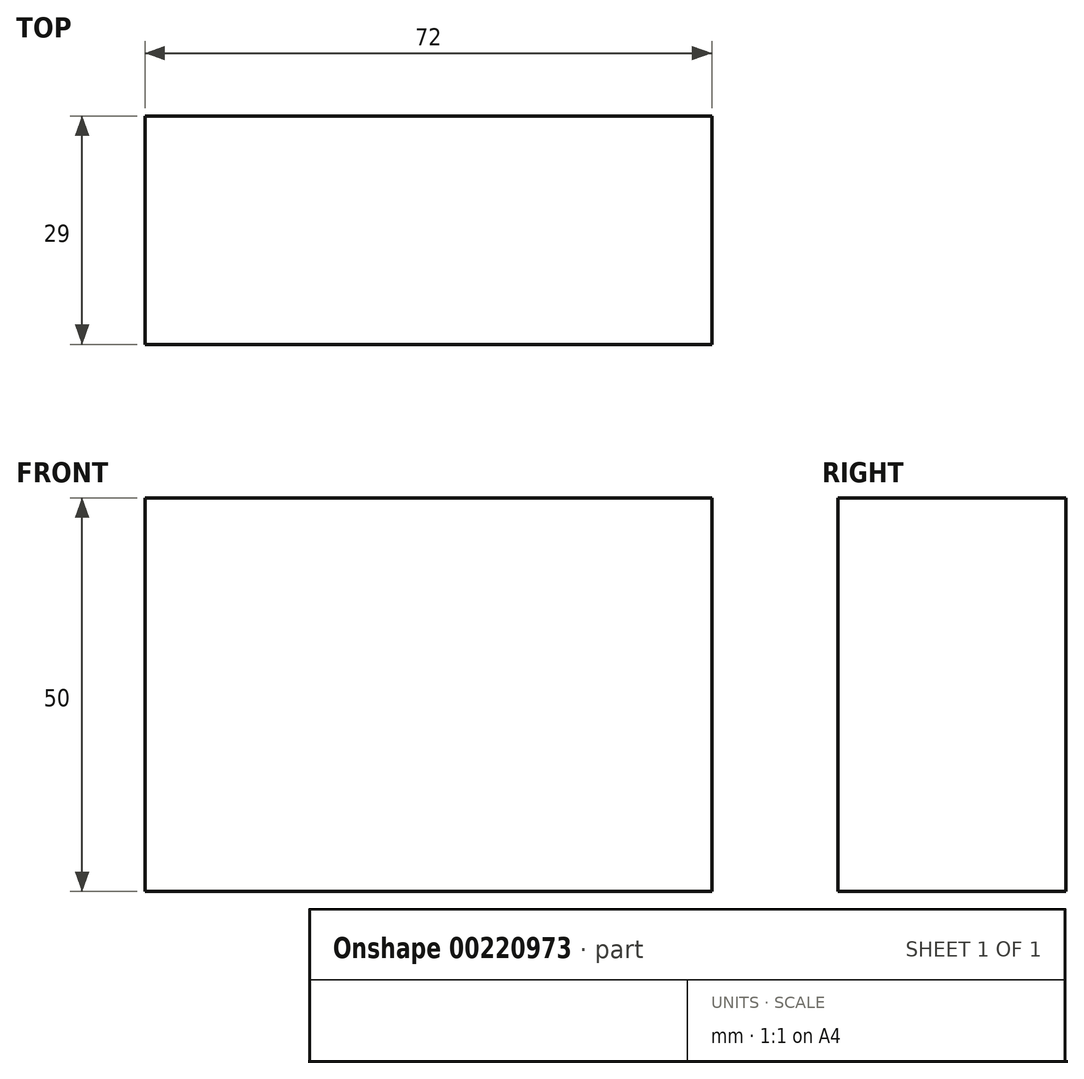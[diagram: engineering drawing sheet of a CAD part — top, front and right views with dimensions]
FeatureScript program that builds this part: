
annotation { "Feature Type Name" : "Feature", "Feature Type Description" : "" }
export const myFeature = defineFeature(function(context is Context, id is Id, definition is map)
    precondition{}
    {
        {
            var Q0;
            Q0=qCreatedBy(makeId("Front.planeOp"),FACE);
            var sketch = newSketch(context, id + "F0", { "sketchPlane" : qUnion([Q0])});
            skLineSegment(sketch, "E0.bottom", {"start": v(0, 0) * mm, "end": v(72, 0) * mm});
            skLineSegment(sketch, "E0.top", {"start": v(0, 50) * mm, "end": v(72, 50) * mm});
            skLineSegment(sketch, "E0.left", {"start": v(0, 0) * mm, "end": v(0, 50) * mm});
            skLineSegment(sketch, "E0.right", {"start": v(72, 0) * mm, "end": v(72, 50) * mm});
            skSolve(sketch);
        }
        {
            var Q0;
            Q0 = qSketchRegion(id + "F0", true);
            extrude(context, id + "F1", {"entities" : qUnion([Q0]), "depth" : 29 * mm, "offsetDistance" : 25 * mm});
        }
    });
